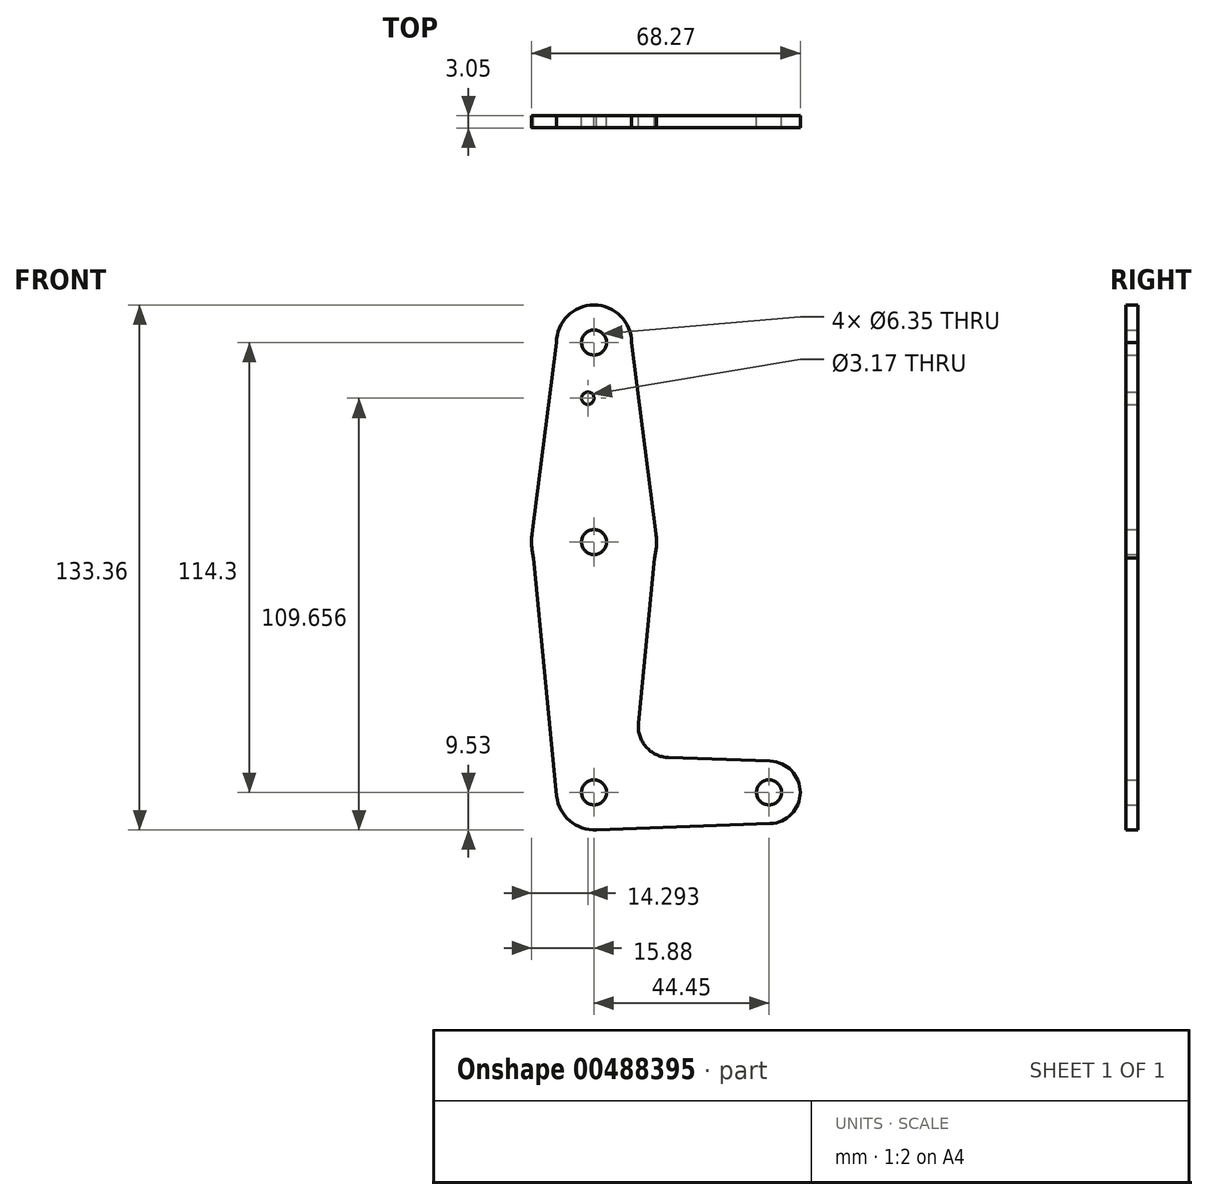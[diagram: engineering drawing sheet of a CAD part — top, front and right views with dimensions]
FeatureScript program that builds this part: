
annotation { "Feature Type Name" : "Feature", "Feature Type Description" : "" }
export const myFeature = defineFeature(function(context is Context, id is Id, definition is map)
    precondition{}
    {
        {
            var Q0;
            Q0=qCreatedBy(makeId("Front.planeOp"),FACE);
            var sketch = newSketch(context, id + "F0", { "sketchPlane" : qUnion([Q0])});
            skCircle(sketch, "E0", {"center": v(0, 114.3) * mm, "radius": 9.53 * mm});
            skCircle(sketch, "E1", {"center": v(0, 63.6) * mm, "radius": 15.88 * mm});
            skCircle(sketch, "E2", {"center": v(0, 0) * mm, "radius": 9.53 * mm});
            skCircle(sketch, "E3", {"center": v(44.45, 0) * mm, "radius": 7.94 * mm});
            skLineSegment(sketch, "E4", {"start": v(-9.53, 114.3) * mm, "end": v(-15.75, 65.61) * mm});
            skLineSegment(sketch, "E5", {"start": v(9.52, 114.3) * mm, "end": v(15.75, 65.61) * mm});
            skLineSegment(sketch, "E6", {"start": v(-15.75, 63.6) * mm, "end": v(-9.48, -0.92) * mm});
            skLineSegment(sketch, "E7", {"start": v(15.75, 63.6) * mm, "end": v(11.28, 17.57) * mm});
            skLineSegment(sketch, "E8", {"start": v(0, 0) * mm, "end": v(44.45, 0) * mm, "construction": true});
            skLineSegment(sketch, "E9", {"start": v(18.9, 8.85) * mm, "end": v(44.73, 7.93) * mm});
            skLineSegment(sketch, "E10", {"start": v(0, -9.53) * mm, "end": v(44.73, -7.93) * mm});
            skLineSegment(sketch, "E11", {"start": v(0, 0) * mm, "end": v(0, 63.6) * mm, "construction": true});
            skLineSegment(sketch, "E12", {"start": v(0, 114.3) * mm, "end": v(0, 63.6) * mm, "construction": true});
            skCircle(sketch, "E13", {"center": v(0, 63.6) * mm, "radius": 3.18 * mm});
            skCircle(sketch, "E14", {"center": v(0, 0) * mm, "radius": 3.18 * mm});
            skCircle(sketch, "E15", {"center": v(44.45, 0) * mm, "radius": 3.18 * mm});
            skCircle(sketch, "E16", {"center": v(0, 114.3) * mm, "radius": 3.18 * mm});
            skCircle(sketch, "E17", {"center": v(-1.59, 100.13) * mm, "radius": 1.59 * mm});
            skArc(sketch, "E18.filletArc", {"start": v(11.28, 17.57) * mm, "mid": v(13.2, 11.56) * mm, "end": v(18.9, 8.85) * mm});
            skSolve(sketch);
        }
        {
            var Q0;
            Q0 = qSketchRegion(id + "F0", true);
            extrude(context, id + "F1", {"entities" : qUnion([Q0]), "depth" : 3.05 * mm});
        }
    });
